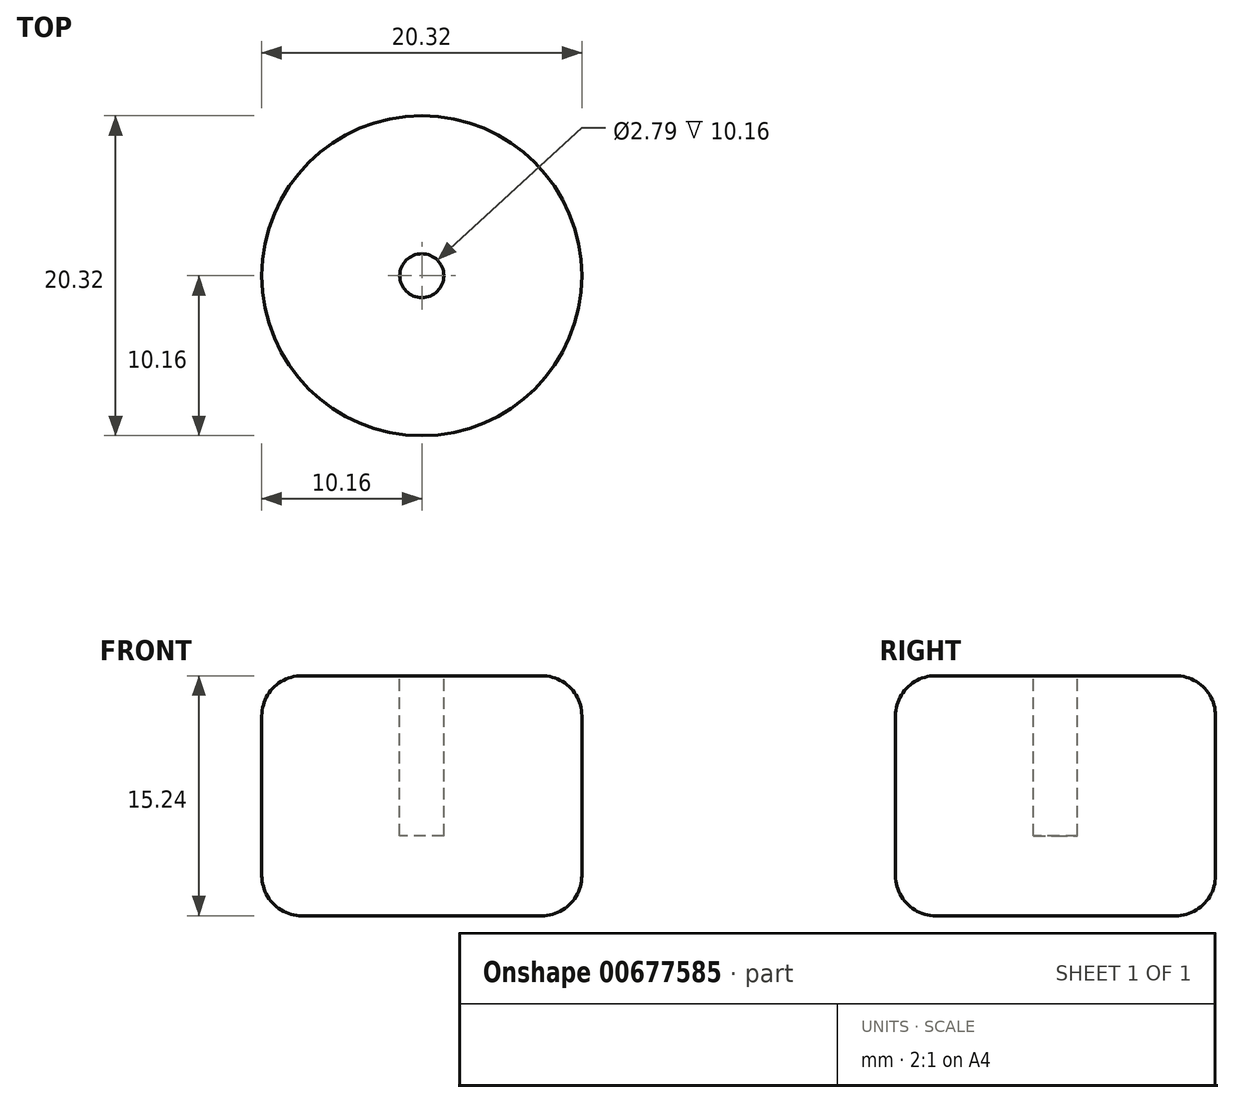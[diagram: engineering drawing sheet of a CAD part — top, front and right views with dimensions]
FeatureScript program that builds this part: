
annotation { "Feature Type Name" : "Feature", "Feature Type Description" : "" }
export const myFeature = defineFeature(function(context is Context, id is Id, definition is map)
    precondition{}
    {
        {
            var Q0;
            Q0=qCreatedBy(makeId("Top.planeOp"),FACE);
            var sketch = newSketch(context, id + "F0", { "sketchPlane" : qUnion([Q0])});
            skCircle(sketch, "E0", {"center": v(0, 0) * mm, "radius": 10.16 * mm});
            skSolve(sketch);
        }
        {
            var Q0;
            Q0=makeQuery(id+"F0.imprint","IMPRINT",FACE,{"disambiguationData":[TD([[makeQuery(id+"F0.imprint","IMPRINT",EDGE,{"derivedFrom":sQuery(id+"F0.wireOp",EDGE,"E0")}),1.0]])]});
            extrude(context, id + "F1", {"entities" : qUnion([Q0]), "depth" : 15.24 * mm, "offsetDistance" : 25.4 * mm});
        }
        {
            var Q0;
            Q0=makeQuery(id+"F1.opExtrude","CAP_EDGE",EDGE,{"disambiguationData":[OSD([sQuery(id+"F0.wireOp",EDGE,"E0")])],"isStart":true});
            var Q1;
            Q1=makeQuery(id+"F1.opExtrude","CAP_EDGE",EDGE,{"disambiguationData":[OSD([sQuery(id+"F0.wireOp",EDGE,"E0")])],"isStart":false});
            fillet(context, id + "F2", {"entities" : qUnion([Q0, Q1]), "radius" : 2.54 * mm, "tangentPropagation" : true, "allowEdgeOverflow" : false});
        }
        {
            var Q0;
            Q0=makeQuery(id+"F1.opExtrude","CAP_FACE",FACE,{"disambiguationData":[OSD([sQuery(id+"F0.wireOp",EDGE,"E0")])],"isStart":false});
            var sketch = newSketch(context, id + "F3", { "sketchPlane" : qUnion([Q0])});
            skCircle(sketch, "E1", {"center": v(0, 0) * mm, "radius": 1.4 * mm});
            skSolve(sketch);
        }
        {
            var Q0;
            Q0=makeQuery(id+"F3.imprint","IMPRINT",FACE,{"disambiguationData":[TD([[makeQuery(id+"F3.imprint","IMPRINT",EDGE,{"derivedFrom":sQuery(id+"F3.wireOp",EDGE,"E1")}),1.0]])]});
            extrude(context, id + "F4", {"entities" : qUnion([Q0]), "operationType" : NewBodyOperationType.REMOVE, "oppositeDirection" : true, "depth" : 10.16 * mm, "offsetDistance" : 25.4 * mm});
        }
    });
